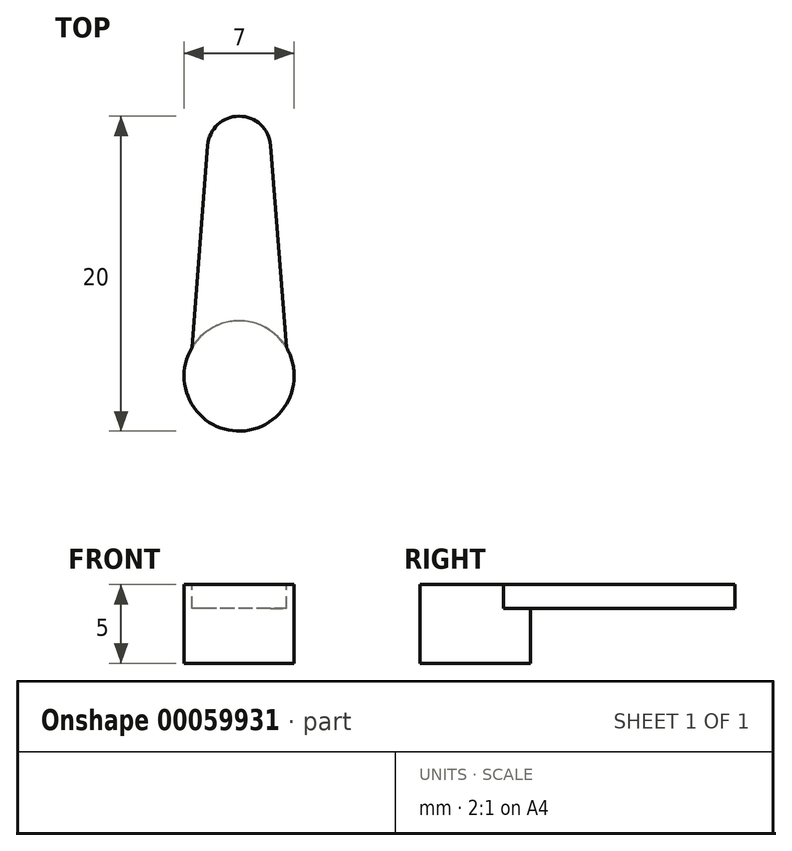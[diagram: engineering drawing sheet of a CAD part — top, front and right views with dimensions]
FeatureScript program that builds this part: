
annotation { "Feature Type Name" : "Feature", "Feature Type Description" : "" }
export const myFeature = defineFeature(function(context is Context, id is Id, definition is map)
    precondition{}
    {
        {
            var Q0;
            Q0=qCreatedBy(makeId("Top.planeOp"),FACE);
            var sketch = newSketch(context, id + "F0", { "sketchPlane" : qUnion([Q0])});
            skCircle(sketch, "E0", {"center": v(0, 0) * mm, "radius": 3.5 * mm});
            skSolve(sketch);
        }
        {
            var Q0;
            Q0 = qSketchRegion(id + "F0", true);
            extrude(context, id + "F1", {"entities" : qUnion([Q0]), "oppositeDirection" : true, "depth" : 5 * mm});
        }
        {
            var Q0;
            Q0=qCreatedBy(makeId("Top.planeOp"),FACE);
            var sketch = newSketch(context, id + "F2", { "sketchPlane" : qUnion([Q0])});
            skArc(sketch, "E1", {"start": v(2, 14.65) * mm, "mid": v(0, 16.5) * mm, "end": v(-2, 14.65) * mm});
            skLineSegment(sketch, "E2", {"start": v(-2, 14.65) * mm, "end": v(-3, 1.8) * mm});
            skLineSegment(sketch, "E3", {"start": v(2, 14.65) * mm, "end": v(3, 1.8) * mm});
            skArc(sketch, "E4", {"start": v(3, 1.8) * mm, "mid": v(0, 3.5) * mm, "end": v(-3, 1.8) * mm});
            skSolve(sketch);
        }
        {
            var Q0;
            Q0=makeQuery(id+"F2.imprint","IMPRINT",FACE,{"disambiguationData":[TD([[makeQuery(id+"F2.imprint","IMPRINT",EDGE,{"derivedFrom":sQuery(id+"F2.wireOp",EDGE,"E1")}),1.0]])]});
            extrude(context, id + "F3", {"entities" : qUnion([Q0]), "operationType" : NewBodyOperationType.ADD, "oppositeDirection" : true, "depth" : 1.5 * mm});
        }
    });
